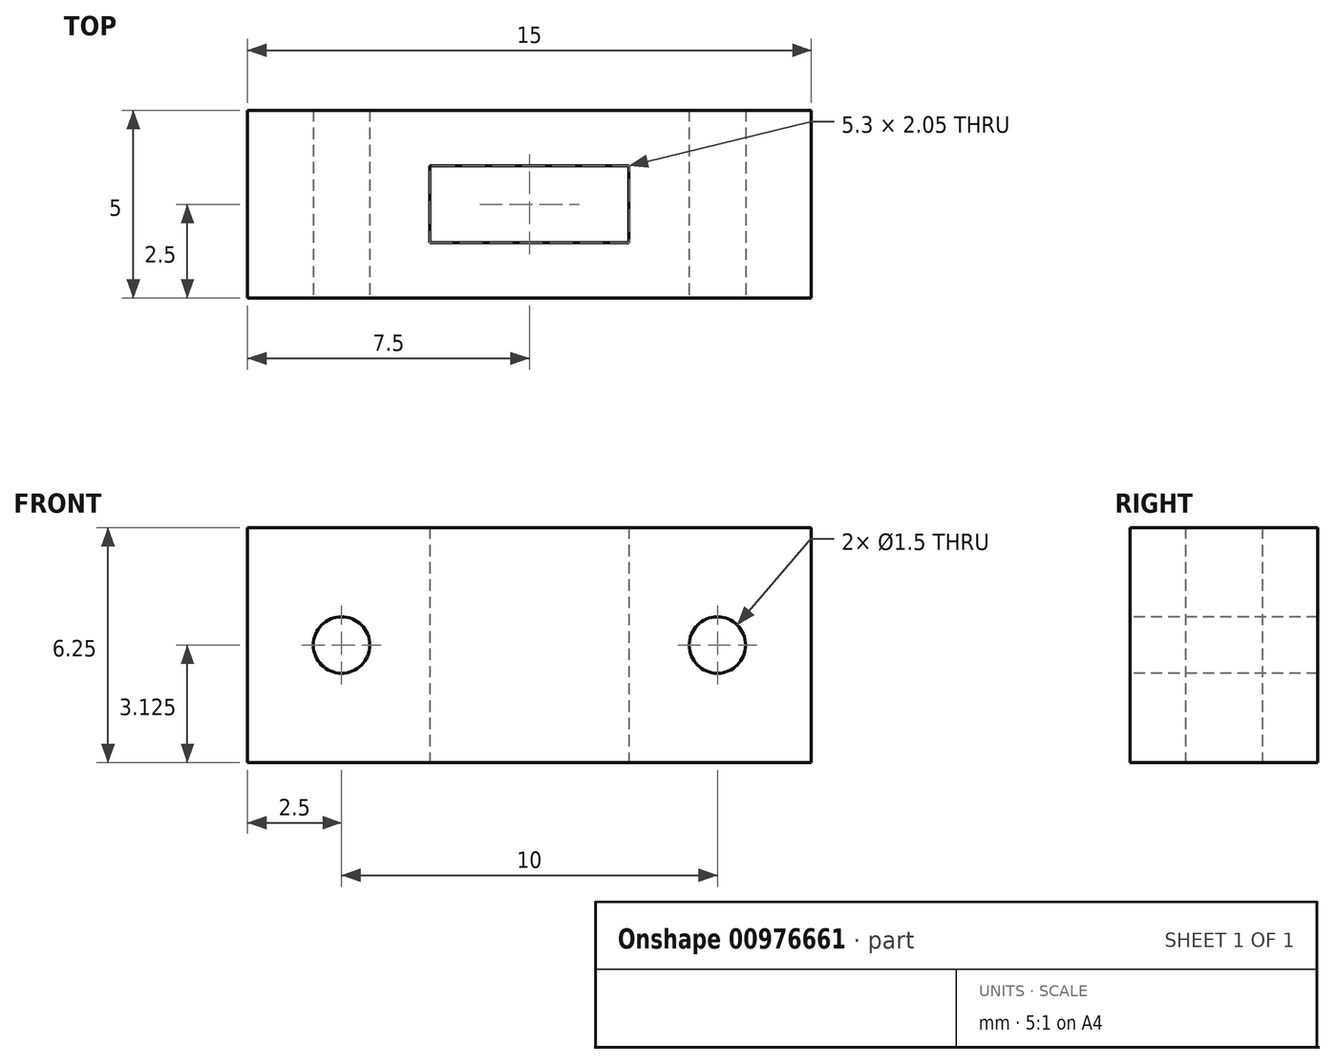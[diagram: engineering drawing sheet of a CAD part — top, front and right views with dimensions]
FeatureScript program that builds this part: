
annotation { "Feature Type Name" : "Feature", "Feature Type Description" : "" }
export const myFeature = defineFeature(function(context is Context, id is Id, definition is map)
    precondition{}
    {
        {
            var Q0;
            Q0=qCreatedBy(makeId("Top.planeOp"),FACE);
            var sketch = newSketch(context, id + "F0", { "sketchPlane" : qUnion([Q0])});
            skLineSegment(sketch, "E0.bottom", {"start": v(7.5, -2.5) * mm, "end": v(-7.5, -2.5) * mm});
            skLineSegment(sketch, "E0.top", {"start": v(7.5, 2.5) * mm, "end": v(-7.5, 2.5) * mm});
            skLineSegment(sketch, "E0.left", {"start": v(7.5, -2.5) * mm, "end": v(7.5, 2.5) * mm});
            skLineSegment(sketch, "E0.right", {"start": v(-7.5, -2.5) * mm, "end": v(-7.5, 2.5) * mm});
            skPoint(sketch, "E0.middle", {"position": v(0, 0) * mm});
            skLineSegment(sketch, "E1.bottom", {"start": v(-2.65, 1.03) * mm, "end": v(2.65, 1.03) * mm});
            skLineSegment(sketch, "E1.top", {"start": v(-2.65, -1.02) * mm, "end": v(2.65, -1.02) * mm});
            skLineSegment(sketch, "E1.left", {"start": v(-2.65, 1.03) * mm, "end": v(-2.65, -1.03) * mm});
            skLineSegment(sketch, "E1.right", {"start": v(2.65, 1.03) * mm, "end": v(2.65, -1.03) * mm});
            skSolve(sketch);
        }
        {
            var Q0;
            Q0 = qSketchRegion(id + "F0", true);
            extrude(context, id + "F1", {"entities" : qUnion([Q0]), "depth" : 6.25 * mm, "offsetDistance" : 25 * mm});
        }
        {
            var Q0;
            Q0=qCreatedBy(makeId("Front.planeOp"),FACE);
            var sketch = newSketch(context, id + "F2", { "sketchPlane" : qUnion([Q0])});
            skCircle(sketch, "E2", {"center": v(-5, 3.12) * mm, "radius": 0.75 * mm});
            skCircle(sketch, "E3", {"center": v(5, 3.12) * mm, "radius": 0.75 * mm});
            skLineSegment(sketch, "E4", {"start": v(-5, 3.12) * mm, "end": v(5, 3.12) * mm, "construction": true});
            skSolve(sketch);
        }
        {
            var Q0;
            Q0 = qSketchRegion(id + "F2", true);
            extrude(context, id + "F3", {"entities" : qUnion([Q0]), "operationType" : NewBodyOperationType.REMOVE, "endBound" : BoundingType.SYMMETRIC, "oppositeDirection" : true, "depth" : 7.8 * mm, "offsetDistance" : 25 * mm});
        }
    });
